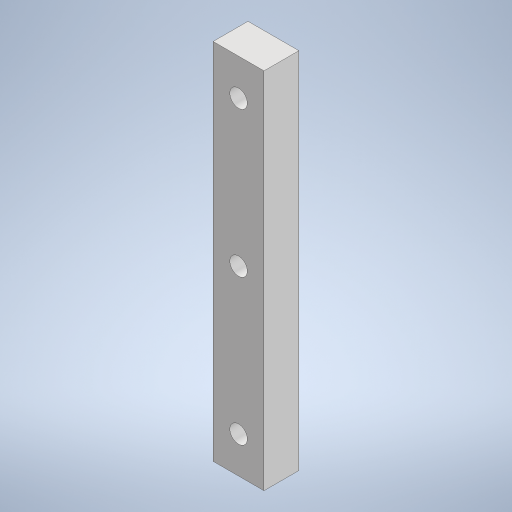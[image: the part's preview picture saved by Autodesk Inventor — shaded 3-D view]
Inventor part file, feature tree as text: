
AUTODESK INVENTOR PART (.ipt)
format: ipt  version: 2024.1 (Build 281209000, 209)  size: 258,560 bytes
history: native  units: in
note: dims shown in document units (in); Inventor stores cm internally (conversion verified against a paired STEP export)
features: extrude x3, sketch x3
ambient origin geometry x8: Origin, YZ Plane, XZ Plane, XY Plane, X Axis, Y Axis, Z Axis, Center Point
bodies: Solid1 (feature_tree)
feature tree (6):
  extrude  "Extrusion1"  Depth=0.2756in
  extrude  "Extrusion2"  Depth=1.9685in
  extrude  "Extrusion3"  Depth=0.0906in
  sketch  "Sketch1"  dims[d0=0.189in d1=0.2756in]
  sketch  "Sketch2"  dims[d2=1.9685in d3=0.0in d4=0.0945in]
  sketch  "Sketch3"  dims[d5=0.1969in d6=0.1378in d7=1.1811in d9=0.7874in d10=0.3937in d12=0.3937in d14=0.0in d15=0.0in d16=0.1654in d17=0.1654in d18=0.1654in d19=0.0906in d20=0.0in]
